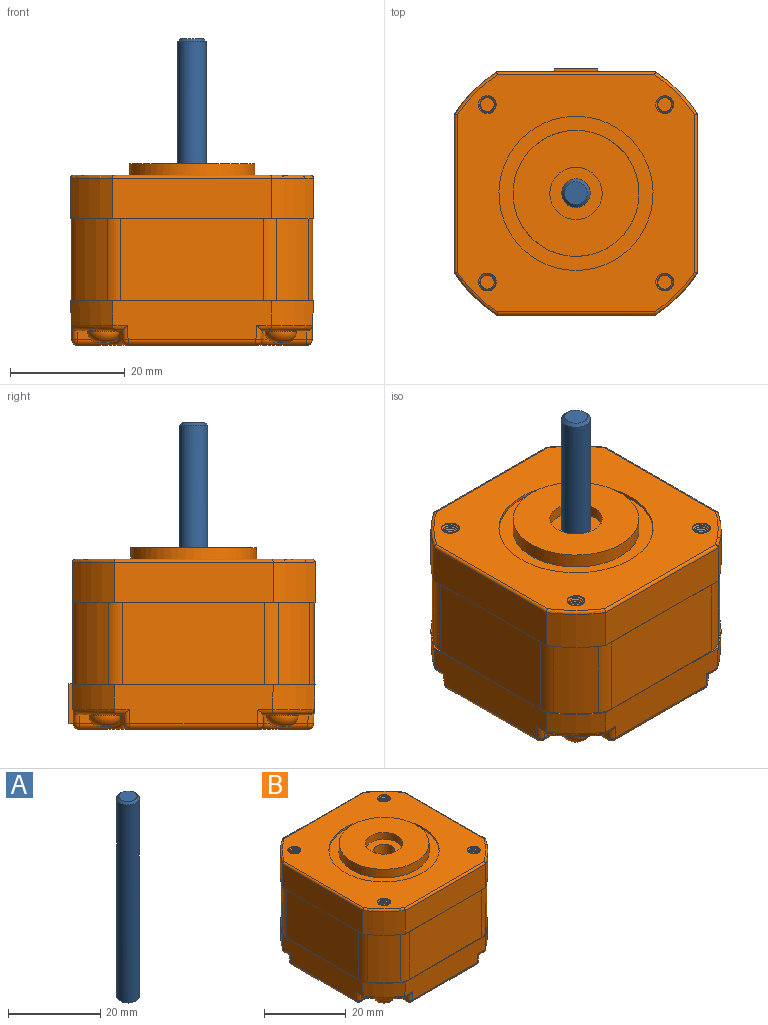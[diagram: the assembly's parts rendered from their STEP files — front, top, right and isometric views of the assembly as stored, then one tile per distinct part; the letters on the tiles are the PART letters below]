
ASSEMBLY  parts=2 mates=1
PART A: 5 faces, bbox 5x5x53.6 mm
  f0: plane 3.98x3.98mm, normal (0,0,1), area 12.4mm2, adj f4
  f1: plane 3.98x3.98mm, normal (0,0,-1), area 12.4mm2, adj f3
  f2: cylinder r=2.5mm len=52.58mm, axis (0,0,1), area 824.4mm2, adj f3,f4
  f3: cone r=2.5mm half-angle=45deg, axis (0,0,1), area 10.1mm2, adj f1,f2
  f4: cone r=1.99mm half-angle=45deg, axis (0,0,-1), area 10.1mm2, adj f0,f2
PART B: 245 faces, bbox 46.1x46.1x31.9 mm
  f0: plane 5.49x4.85mm, normal (0,1,0), area 22.5mm2, adj f228,f229,f230,f231,f232,f233,f237,f239
  f1: plane 27.77x6.84mm, normal (0,1,-0.03), area 121.2mm2, adj f4,f5,f60,f62,f65,f80,f81,f87
  f2: plane 1.69x0.25mm, normal (0,0,-1), area 0.4mm2, adj f6,f46,f222,f226
  f3: plane 1.69x0.25mm, normal (0,0,-1), area 0.4mm2, adj f7,f46,f223,f227
  f4: plane 1.59x0.25mm, normal (0,0,1), area 0.4mm2, adj f1,f6,f222,f226
  f5: plane 1.59x0.25mm, normal (0,0,1), area 0.4mm2, adj f1,f7,f223,f227
  f6: plane 6.61x0.25mm, normal (0,1,0), area 1.7mm2, adj f2,f4,f222,f226
  f7: plane 6.61x0.25mm, normal (0,1,0), area 1.7mm2, adj f3,f5,f223,f227
  f8: plane 0.62x0.62mm, normal (0,0,-1), area 0.3mm2, adj f181,f214,f215
  f9: plane 0.62x0.62mm, normal (0,0,-1), area 0.3mm2, adj f181,f216,f217
  f10: plane 0.62x0.62mm, normal (0,0,-1), area 0.3mm2, adj f181,f218,f219
  f11: plane 0.62x0.62mm, normal (0,0,-1), area 0.3mm2, adj f177,f201,f202
  f12: plane 0.62x0.62mm, normal (0,0,-1), area 0.3mm2, adj f177,f203,f204
  f13: plane 0.62x0.62mm, normal (0,0,-1), area 0.3mm2, adj f177,f205,f206
  f14: plane 0.62x0.62mm, normal (0,0,-1), area 0.3mm2, adj f173,f188,f189
  f15: plane 0.62x0.62mm, normal (0,0,-1), area 0.3mm2, adj f173,f190,f191
  f16: plane 0.62x0.62mm, normal (0,0,-1), area 0.3mm2, adj f173,f192,f193
  f17: plane 7.81x7.81mm, normal (0,0,-1), area 17.4mm2, adj f74,f75,f76,f80,f81,f83,f86,f90
  f18: plane 7.81x7.81mm, normal (0,0,-1), area 17.4mm2, adj f77,f78,f79,f97,f101,f105,f108,f113
  f19: plane 7.81x7.81mm, normal (0,0,-1), area 17.4mm2, adj f68,f69,f70,f87,f91,f94,f98,f102
  f20: plane 41.4x41.4mm, normal (0,0,1), area 1030.3mm2, adj f36,f37,f38,f39,f40,f41,f42,f43
  f21: plane 0.62x0.62mm, normal (0,0,-1), area 0.3mm2, adj f138,f145,f146
  f22: plane 0.62x0.62mm, normal (0,0,-1), area 0.3mm2, adj f138,f147,f148
  f23: plane 0.62x0.62mm, normal (0,0,-1), area 0.3mm2, adj f138,f149,f150
  f24: plane 7.81x7.81mm, normal (0,0,-1), area 17.4mm2, adj f71,f72,f73,f109,f110,f114,f117,f120
  f25: plane 39.91x39.91mm, normal (0,0,-1), area 1280.7mm2, adj f82,f85,f88,f89,f95,f96,f99,f103
  f26: plane 22x22mm, normal (0,0,1), area 314.3mm2, adj f124,f127
  f27: plane 42.42x42.42mm, normal (0,0,-1), area 24.6mm2, adj f28,f29,f30,f31,f32,f33,f34,f35
  f28: cylinder r=25.35mm len=7.33mm, axis (0,0,1), area 73.7mm2, adj f27,f29,f35,f42
  f29: plane 27.77x7.06mm, normal (0,1,0), area 196.1mm2, adj f27,f28,f30,f43
  f30: cylinder r=25.35mm len=7.33mm, axis (0,0,1), area 73.7mm2, adj f27,f29,f31,f41
  f31: plane 27.77x7.06mm, normal (1,0,0), area 196.1mm2, adj f27,f30,f32,f39
  f32: cylinder r=25.35mm len=7.33mm, axis (0,0,1), area 73.7mm2, adj f27,f31,f33,f37
  f33: plane 27.77x7.06mm, normal (0,-1,0), area 196.1mm2, adj f27,f32,f34,f36
  f34: cylinder r=25.35mm len=7.33mm, axis (0,0,1), area 73.7mm2, adj f27,f33,f35,f38
  f35: plane 27.77x7.06mm, normal (-1,0,0), area 196.1mm2, adj f27,f28,f34,f40
  f36: cylinder r=0.51mm len=27.77mm, axis (1,0,0), area 22mm2, adj f20,f33,f37,f38
  f37: torus R=24.84mm, axis (0,0,1), area 8.1mm2, adj f20,f32,f36,f39
  f38: torus R=24.84mm, axis (0,0,1), area 8.1mm2, adj f20,f34,f36,f40
  f39: cylinder r=0.51mm len=27.77mm, axis (0,1,0), area 22mm2, adj f20,f31,f37,f41
  f40: cylinder r=0.51mm len=27.77mm, axis (0,-1,0), area 22mm2, adj f20,f35,f38,f42
  f41: torus R=24.84mm, axis (0,0,1), area 8.1mm2, adj f20,f30,f39,f43
  f42: torus R=24.84mm, axis (0,0,1), area 8.1mm2, adj f20,f28,f40,f43
  f43: cylinder r=0.51mm len=27.77mm, axis (-1,0,0), area 22mm2, adj f20,f29,f41,f42
  f44: cylinder r=25.13mm len=14.33mm, axis (0,0,1), area 112.4mm2, adj f27,f45,f58,f60
  f45: cylinder r=4.01mm len=14.33mm, axis (0,0,1), area 36.2mm2, adj f27,f44,f46,f60
  f46: plane 24.85x14.33mm, normal (0,1,0), area 356mm2, adj f2,f3,f27,f45,f47,f60,f224
  f47: cylinder r=4.01mm len=14.33mm, axis (0,0,1), area 36.2mm2, adj f27,f46,f48,f60
  f48: cylinder r=25.13mm len=14.33mm, axis (0,0,1), area 112.4mm2, adj f27,f47,f49,f60
  f49: cylinder r=4.01mm len=14.33mm, axis (0,0,1), area 36.2mm2, adj f27,f48,f50,f60
  f50: plane 24.85x14.33mm, normal (1,0,0), area 356mm2, adj f27,f49,f51,f60
  f51: cylinder r=4.01mm len=14.33mm, axis (0,0,1), area 36.2mm2, adj f27,f50,f52,f60
  f52: cylinder r=25.13mm len=14.33mm, axis (0,0,1), area 112.4mm2, adj f27,f51,f53,f60
  f53: cylinder r=4.01mm len=14.33mm, axis (0,0,1), area 36.2mm2, adj f27,f52,f54,f60
  f54: plane 24.85x14.33mm, normal (0,-1,0), area 356mm2, adj f27,f53,f55,f60
  f55: cylinder r=4.01mm len=14.33mm, axis (0,0,1), area 36.2mm2, adj f27,f54,f56,f60
  f56: cylinder r=25.13mm len=14.33mm, axis (0,0,1), area 112.4mm2, adj f27,f55,f57,f60
  f57: cylinder r=4.01mm len=14.33mm, axis (0,0,1), area 36.2mm2, adj f27,f56,f59,f60
  f58: cylinder r=4.01mm len=14.33mm, axis (0,0,1), area 36.2mm2, adj f27,f44,f59,f60
  f59: plane 24.85x14.33mm, normal (-1,0,0), area 356mm2, adj f27,f57,f58,f60
  f60: plane 42.42x42.42mm, normal (0,0,1), area 23.6mm2, adj f1,f44,f45,f46,f47,f48,f49,f50
  f61: cone r=25.35mm half-angle=2deg, axis (0,0,1), area 44.6mm2, adj f60,f64,f67,f105
  f62: cone r=25.35mm half-angle=2deg, axis (0,0,1), area 44.6mm2, adj f1,f60,f64,f83
  f63: cone r=25.35mm half-angle=2deg, axis (0,0,1), area 44.6mm2, adj f60,f66,f67,f114
  f64: plane 27.77x6.84mm, normal (-1,0,-0.03), area 176.3mm2, adj f60,f61,f62,f86,f90,f96,f97,f101
  f65: cone r=25.35mm half-angle=2deg, axis (0,0,1), area 44.6mm2, adj f1,f60,f66,f94
  f66: plane 27.77x6.84mm, normal (1,0,-0.03), area 176.3mm2, adj f60,f63,f65,f98,f102,f109,f110,f111
  f67: plane 27.77x6.84mm, normal (0,-1,-0.03), area 176.3mm2, adj f60,f61,f63,f108,f113,f117,f119,f120
  f68: plane 4.47x1.56mm, normal (0,1,-0.03), area 6.9mm2, adj f19,f69,f102,f103
  f69: cone r=3.3mm half-angle=2deg, axis (0,0,-1), area 8.2mm2, adj f19,f68,f70,f99
  f70: plane 4.47x1.56mm, normal (1,0,-0.03), area 6.9mm2, adj f19,f69,f87,f95
  f71: plane 4.47x1.56mm, normal (1,0,-0.03), area 6.9mm2, adj f24,f72,f120,f123
  f72: cone r=3.3mm half-angle=2deg, axis (0,0,-1), area 8.2mm2, adj f24,f71,f73,f121
  f73: plane 4.47x1.56mm, normal (0,-1,-0.03), area 6.9mm2, adj f24,f72,f110,f118
  f74: plane 4.47x1.56mm, normal (-1,0,-0.03), area 6.9mm2, adj f17,f75,f81,f82
  f75: cone r=3.3mm half-angle=2deg, axis (0,0,-1), area 8.2mm2, adj f17,f74,f76,f85
  f76: plane 4.47x1.56mm, normal (0,1,-0.03), area 6.9mm2, adj f17,f75,f89,f90
  f77: cone r=3.3mm half-angle=2deg, axis (0,0,-1), area 8.2mm2, adj f18,f78,f79,f107
  f78: plane 4.47x1.56mm, normal (-1,0,-0.03), area 6.9mm2, adj f18,f77,f112,f113
  f79: plane 4.47x1.56mm, normal (0,-1,-0.03), area 6.9mm2, adj f18,f77,f97,f104
  f80: cylinder r=1.02mm len=2.58mm, axis (-1,0,0), area 3mm2, adj f1,f17,f81,f83
  f81: cylinder r=1.02mm len=2.55mm, axis (-0.03,0.03,1), area 3.1mm2, adj f1,f17,f74,f80,f84
  f82: cylinder r=1.02mm len=4.42mm, axis (0,1,0), area 6.9mm2, adj f25,f74,f84,f85
  f83: torus R=24.18mm, axis (0,0,-1), area 15.3mm2, adj f17,f62,f80,f86,f179
  f84: sphere r=1.02mm, area 1.6mm2, adj f81,f82,f88
  f85: torus R=4.37mm, axis (0,0,1), area 9.2mm2, adj f25,f75,f82,f89
  f86: cylinder r=1.02mm len=2.58mm, axis (0,-1,0), area 3mm2, adj f17,f64,f83,f90
  f87: cylinder r=1.02mm len=2.55mm, axis (-0.03,-0.03,-1), area 3.1mm2, adj f1,f19,f70,f91,f92
  f88: cylinder r=1.02mm len=22.33mm, axis (1,0,0), area 34.9mm2, adj f1,f25,f84,f92
  f89: cylinder r=1.02mm len=4.42mm, axis (1,0,0), area 6.9mm2, adj f25,f76,f85,f93
  f90: cylinder r=1.02mm len=2.55mm, axis (0.03,-0.03,-1), area 3.1mm2, adj f17,f64,f76,f86,f93
  f91: cylinder r=1.02mm len=2.58mm, axis (-1,0,0), area 3mm2, adj f1,f19,f87,f94
  f92: sphere r=1.02mm, area 1.6mm2, adj f87,f88,f95
  f93: sphere r=1.02mm, area 1.6mm2, adj f89,f90,f96
  f94: torus R=24.18mm, axis (0,0,1), area 15.3mm2, adj f19,f65,f91,f98,f171
  f95: cylinder r=1.02mm len=4.42mm, axis (0,-1,0), area 6.9mm2, adj f25,f70,f92,f99
  f96: cylinder r=1.02mm len=22.33mm, axis (0,1,0), area 34.9mm2, adj f25,f64,f93,f100
  f97: cylinder r=1.02mm len=2.55mm, axis (-0.03,-0.03,1), area 3.1mm2, adj f18,f64,f79,f100,f101
  f98: cylinder r=1.02mm len=2.58mm, axis (0,1,0), area 3mm2, adj f19,f66,f94,f102
  f99: torus R=4.37mm, axis (0,0,1), area 9.2mm2, adj f25,f69,f95,f103
  f100: sphere r=1.02mm, area 1.6mm2, adj f96,f97,f104
  f101: cylinder r=1.02mm len=2.58mm, axis (0,-1,0), area 3mm2, adj f18,f64,f97,f105
  f102: cylinder r=1.02mm len=2.55mm, axis (0.03,0.03,1), area 3.1mm2, adj f19,f66,f68,f98,f106
  f103: cylinder r=1.02mm len=4.42mm, axis (1,0,0), area 6.9mm2, adj f25,f68,f99,f106
  f104: cylinder r=1.02mm len=4.42mm, axis (-1,0,0), area 6.9mm2, adj f25,f79,f100,f107
  f105: torus R=24.18mm, axis (0,0,-1), area 15.3mm2, adj f18,f61,f101,f108,f175
  f106: sphere r=1.02mm, area 1.6mm2, adj f102,f103,f111
  f107: torus R=4.37mm, axis (0,0,1), area 9.2mm2, adj f25,f77,f104,f112
  f108: cylinder r=1.02mm len=2.58mm, axis (1,0,0), area 3mm2, adj f18,f67,f105,f113
  f109: cylinder r=1.02mm len=2.58mm, axis (0,1,0), area 3mm2, adj f24,f66,f110,f114
  f110: cylinder r=1.02mm len=2.55mm, axis (-0.03,0.03,-1), area 3.1mm2, adj f24,f66,f73,f109,f115
  f111: cylinder r=1.02mm len=22.33mm, axis (0,-1,0), area 34.9mm2, adj f25,f66,f106,f115
  f112: cylinder r=1.02mm len=4.42mm, axis (0,1,0), area 6.9mm2, adj f25,f78,f107,f116
  f113: cylinder r=1.02mm len=2.55mm, axis (0.03,0.03,-1), area 3.1mm2, adj f18,f67,f78,f108,f116
  f114: torus R=24.18mm, axis (0,0,-1), area 15.3mm2, adj f24,f63,f109,f117,f136
  f115: sphere r=1.02mm, area 1.6mm2, adj f110,f111,f118
  f116: sphere r=1.02mm, area 1.6mm2, adj f112,f113,f119
  f117: cylinder r=1.02mm len=2.58mm, axis (1,0,0), area 3mm2, adj f24,f67,f114,f120
  f118: cylinder r=1.02mm len=4.42mm, axis (-1,0,0), area 6.9mm2, adj f25,f73,f115,f121
  f119: cylinder r=1.02mm len=22.33mm, axis (-1,0,0), area 34.9mm2, adj f25,f67,f116,f122
  f120: cylinder r=1.02mm len=2.55mm, axis (0.03,-0.03,1), area 3.1mm2, adj f24,f67,f71,f117,f122
  f121: torus R=4.37mm, axis (0,0,1), area 9.2mm2, adj f25,f72,f118,f123
  f122: sphere r=1.02mm, area 1.6mm2, adj f119,f120,f123
  f123: cylinder r=1.02mm len=4.42mm, axis (0,-1,0), area 6.9mm2, adj f25,f71,f121,f122
  f124: cylinder r=11mm len=22mm, axis (0,0,-1), area 175.5mm2, adj f26,f128
  f125: cylinder r=2.5mm len=29.72mm, axis (0,0,1), area 466mm2, adj f25,f126
  f126: plane 9.14x9.14mm, normal (0,0,1), area 46.1mm2, adj f125,f127
  f127: cylinder r=4.57mm len=9.14mm, axis (0,0,1), area 58.4mm2, adj f26,f126
  f128: plane 26.92x26.92mm, normal (0,0,1), area 189.3mm2, adj f124,f129
  f129: cylinder r=13.46mm len=26.92mm, axis (0,0,1), area 43mm2, adj f20,f128
  f130: cone r=1.55mm half-angle=45deg, axis (0,0,1), area 2.6mm2, adj f20,f132,f133,f134,f135
  f131: plane 2.87x2.83mm, normal (0,0,1), area 5.7mm2, adj f132,f133,f134,f135
  f132: bspline ~4.01x3.53mm, area 19.4mm2, adj f130,f131,f133,f135
  f133: bspline ~3.88x2.84mm, area 6.7mm2, adj f130,f131,f132,f134
  f134: bspline ~4.17x3.53mm, area 19.4mm2, adj f130,f131,f133,f135
  f135: cylinder r=1.5mm len=3.76mm, axis (0,0,1), area 7.3mm2, adj f130,f131,f132,f134
  f136: plane 2.3x2.3mm, normal (0,0,1), area 1.1mm2, adj f114,f137
  f137: cylinder r=2.75mm len=5.5mm, axis (0,0,1), area 2.2mm2, adj f24,f136,f138
  f138: torus R=0.84mm, axis (0,0,1), area 37.5mm2, adj f21,f22,f23,f137,f139,f140,f141,f142
  f139: plane 0.62x0.62mm, normal (0,0,-1), area 0.3mm2, adj f138,f144,f151
  f140: plane 1.41x0.41mm, normal (0,-1,0), area 0.6mm2, adj f138,f144,f145,f152
  f141: plane 1.41x0.41mm, normal (1,0,0), area 0.6mm2, adj f138,f146,f147,f152
  f142: plane 1.41x0.41mm, normal (0,1,0), area 0.6mm2, adj f138,f148,f149,f152
  f143: plane 1.42x0.41mm, normal (-1,0,0), area 0.6mm2, adj f138,f150,f151,f152
  f144: plane 1.56x1.34mm, normal (-1,0,0), area 1.9mm2, adj f138,f139,f140,f151,f152
  f145: plane 1.56x1.33mm, normal (1,0,0), area 1.9mm2, adj f21,f138,f140,f146,f152
  f146: plane 1.56x1.34mm, normal (0,-1,0), area 1.9mm2, adj f21,f138,f141,f145,f152
  f147: plane 1.56x1.33mm, normal (0,1,0), area 1.9mm2, adj f22,f138,f141,f148,f152
  f148: plane 1.56x1.34mm, normal (1,0,0), area 1.9mm2, adj f22,f138,f142,f147,f152
  f149: plane 1.56x1.33mm, normal (-1,0,0), area 1.9mm2, adj f23,f138,f142,f150,f152
  f150: plane 1.56x1.34mm, normal (0,1,0), area 1.9mm2, adj f23,f138,f143,f149,f152
  f151: plane 1.56x1.33mm, normal (0,-1,0), area 1.9mm2, adj f138,f139,f143,f144,f152
  f152: plane 3x3mm, normal (0,0,-1), area 2.3mm2, adj f140,f141,f142,f143,f144,f145,f146,f147
  f153: cone r=1.55mm half-angle=45deg, axis (0,0,1), area 2.6mm2, adj f20,f155,f156,f157,f158
  f154: plane 2.87x2.83mm, normal (0,0,1), area 5.7mm2, adj f155,f156,f157,f158
  f155: bspline ~4.01x3.53mm, area 19.4mm2, adj f153,f154,f156,f158
  f156: bspline ~3.88x2.84mm, area 6.7mm2, adj f153,f154,f155,f157
  f157: bspline ~4.17x3.53mm, area 19.4mm2, adj f153,f154,f156,f158
  f158: cylinder r=1.5mm len=3.76mm, axis (0,0,1), area 7.3mm2, adj f153,f154,f155,f157
  f159: cone r=1.55mm half-angle=45deg, axis (0,0,1), area 2.6mm2, adj f20,f161,f162,f163,f164
  f160: plane 2.87x2.83mm, normal (0,0,1), area 5.7mm2, adj f161,f162,f163,f164
  f161: bspline ~4.01x3.53mm, area 19.4mm2, adj f159,f160,f162,f164
  f162: bspline ~3.88x2.84mm, area 6.7mm2, adj f159,f160,f161,f163
  f163: bspline ~4.17x3.53mm, area 19.4mm2, adj f159,f160,f162,f164
  f164: cylinder r=1.5mm len=3.76mm, axis (0,0,1), area 7.3mm2, adj f159,f160,f161,f163
  f165: cone r=1.55mm half-angle=45deg, axis (0,0,1), area 2.6mm2, adj f20,f167,f168,f169,f170
  f166: plane 2.87x2.83mm, normal (0,0,1), area 5.7mm2, adj f167,f168,f169,f170
  f167: bspline ~4.01x3.53mm, area 19.4mm2, adj f165,f166,f168,f170
  f168: bspline ~3.88x2.84mm, area 6.7mm2, adj f165,f166,f167,f169
  f169: bspline ~4.17x3.53mm, area 19.4mm2, adj f165,f166,f168,f170
  f170: cylinder r=1.5mm len=3.76mm, axis (0,0,1), area 7.3mm2, adj f165,f166,f167,f169
  f171: plane 2.3x2.3mm, normal (0,0,1), area 1.1mm2, adj f94,f172
  f172: cylinder r=2.75mm len=5.5mm, axis (0,0,1), area 2.2mm2, adj f19,f171,f173
  f173: torus R=0.84mm, axis (0,0,1), area 37.5mm2, adj f14,f15,f16,f172,f174,f183,f184,f185
  f174: plane 0.62x0.62mm, normal (0,0,-1), area 0.3mm2, adj f173,f187,f194
  f175: plane 2.3x2.3mm, normal (0,0,1), area 1.1mm2, adj f105,f176
  f176: cylinder r=2.75mm len=5.5mm, axis (0,0,1), area 2.2mm2, adj f18,f175,f177
  f177: torus R=0.84mm, axis (0,0,1), area 37.5mm2, adj f11,f12,f13,f176,f178,f196,f197,f198
  f178: plane 0.62x0.62mm, normal (0,0,-1), area 0.3mm2, adj f177,f200,f207
  f179: plane 2.3x2.3mm, normal (0,0,1), area 1.1mm2, adj f83,f180
  f180: cylinder r=2.75mm len=5.5mm, axis (0,0,1), area 2.2mm2, adj f17,f179,f181
  f181: torus R=0.84mm, axis (0,0,1), area 37.5mm2, adj f8,f9,f10,f180,f182,f209,f210,f211
  f182: plane 0.62x0.62mm, normal (0,0,-1), area 0.3mm2, adj f181,f213,f220
  f183: plane 1.41x0.41mm, normal (0,-1,0), area 0.6mm2, adj f173,f187,f188,f195
  f184: plane 1.41x0.41mm, normal (1,0,0), area 0.6mm2, adj f173,f189,f190,f195
  f185: plane 1.41x0.41mm, normal (0,1,0), area 0.6mm2, adj f173,f191,f192,f195
  f186: plane 1.42x0.41mm, normal (-1,0,0), area 0.6mm2, adj f173,f193,f194,f195
  f187: plane 1.56x1.34mm, normal (-1,0,0), area 1.9mm2, adj f173,f174,f183,f194,f195
  f188: plane 1.56x1.33mm, normal (1,0,0), area 1.9mm2, adj f14,f173,f183,f189,f195
  f189: plane 1.56x1.34mm, normal (0,-1,0), area 1.9mm2, adj f14,f173,f184,f188,f195
  f190: plane 1.56x1.33mm, normal (0,1,0), area 1.9mm2, adj f15,f173,f184,f191,f195
  f191: plane 1.56x1.34mm, normal (1,0,0), area 1.9mm2, adj f15,f173,f185,f190,f195
  f192: plane 1.56x1.33mm, normal (-1,0,0), area 1.9mm2, adj f16,f173,f185,f193,f195
  f193: plane 1.56x1.34mm, normal (0,1,0), area 1.9mm2, adj f16,f173,f186,f192,f195
  f194: plane 1.56x1.33mm, normal (0,-1,0), area 1.9mm2, adj f173,f174,f186,f187,f195
  f195: plane 3x3mm, normal (0,0,-1), area 2.3mm2, adj f183,f184,f185,f186,f187,f188,f189,f190
  f196: plane 1.41x0.41mm, normal (0,-1,0), area 0.6mm2, adj f177,f200,f201,f208
  f197: plane 1.41x0.41mm, normal (1,0,0), area 0.6mm2, adj f177,f202,f203,f208
  f198: plane 1.41x0.41mm, normal (0,1,0), area 0.6mm2, adj f177,f204,f205,f208
  f199: plane 1.42x0.41mm, normal (-1,0,0), area 0.6mm2, adj f177,f206,f207,f208
  f200: plane 1.56x1.34mm, normal (-1,0,0), area 1.9mm2, adj f177,f178,f196,f207,f208
  f201: plane 1.56x1.33mm, normal (1,0,0), area 1.9mm2, adj f11,f177,f196,f202,f208
  f202: plane 1.56x1.34mm, normal (0,-1,0), area 1.9mm2, adj f11,f177,f197,f201,f208
  f203: plane 1.56x1.33mm, normal (0,1,0), area 1.9mm2, adj f12,f177,f197,f204,f208
  f204: plane 1.56x1.34mm, normal (1,0,0), area 1.9mm2, adj f12,f177,f198,f203,f208
  f205: plane 1.56x1.33mm, normal (-1,0,0), area 1.9mm2, adj f13,f177,f198,f206,f208
  f206: plane 1.56x1.34mm, normal (0,1,0), area 1.9mm2, adj f13,f177,f199,f205,f208
  f207: plane 1.56x1.33mm, normal (0,-1,0), area 1.9mm2, adj f177,f178,f199,f200,f208
  f208: plane 3x3mm, normal (0,0,-1), area 2.3mm2, adj f196,f197,f198,f199,f200,f201,f202,f203
  f209: plane 1.41x0.41mm, normal (0,-1,0), area 0.6mm2, adj f181,f213,f214,f221
  f210: plane 1.41x0.41mm, normal (1,0,0), area 0.6mm2, adj f181,f215,f216,f221
  f211: plane 1.41x0.41mm, normal (0,1,0), area 0.6mm2, adj f181,f217,f218,f221
  f212: plane 1.42x0.41mm, normal (-1,0,0), area 0.6mm2, adj f181,f219,f220,f221
  f213: plane 1.56x1.34mm, normal (-1,0,0), area 1.9mm2, adj f181,f182,f209,f220,f221
  f214: plane 1.56x1.33mm, normal (1,0,0), area 1.9mm2, adj f8,f181,f209,f215,f221
  f215: plane 1.56x1.34mm, normal (0,-1,0), area 1.9mm2, adj f8,f181,f210,f214,f221
  f216: plane 1.56x1.33mm, normal (0,1,0), area 1.9mm2, adj f9,f181,f210,f217,f221
  f217: plane 1.56x1.34mm, normal (1,0,0), area 1.9mm2, adj f9,f181,f211,f216,f221
  f218: plane 1.56x1.33mm, normal (-1,0,0), area 1.9mm2, adj f10,f181,f211,f219,f221
  f219: plane 1.56x1.34mm, normal (0,1,0), area 1.9mm2, adj f10,f181,f212,f218,f221
  f220: plane 1.56x1.33mm, normal (0,-1,0), area 1.9mm2, adj f181,f182,f212,f213,f221
  f221: plane 3x3mm, normal (0,0,-1), area 2.3mm2, adj f209,f210,f211,f212,f213,f214,f215,f216
  f222: plane 6.61x1.82mm, normal (1,0,0), area 11.2mm2, adj f1,f2,f4,f6,f60
  f223: plane 6.61x1.82mm, normal (-1,0,0), area 11.2mm2, adj f1,f3,f5,f7,f60
  f224: plane 7.62x0.13mm, normal (0,0,1), area 1mm2, adj f46,f226,f227,f234
  f225: plane 7.62x6.99mm, normal (0,1,0), area 27.8mm2, adj f226,f227,f228,f229,f230,f231,f232,f233
  f226: plane 6.99x2.36mm, normal (-1,0,0), area 15.9mm2, adj f1,f2,f4,f6,f224,f225,f234,f235
  f227: plane 6.99x2.36mm, normal (1,0,0), area 15.9mm2, adj f1,f3,f5,f7,f224,f225,f234,f235
  f228: plane 4.41x2.36mm, normal (0,0,-1), area 10.4mm2, adj f0,f225,f229,f233
  f229: plane 2.36x1.08mm, normal (-0.71,0,-0.71), area 3.6mm2, adj f0,f225,f228,f230
  f230: plane 3.77x2.36mm, normal (-1,0,0), area 8.9mm2, adj f0,f225,f229,f231
  f231: plane 4.41x2.36mm, normal (0,0,1), area 10.4mm2, adj f0,f225,f230,f232
  f232: plane 2.36x1.08mm, normal (0.71,0,0.71), area 3.6mm2, adj f0,f225,f231,f233
  f233: plane 3.77x2.36mm, normal (1,0,0), area 8.9mm2, adj f0,f225,f228,f232
  f234: plane 7.62x0.19mm, normal (0,-1,0.03), area 1.4mm2, adj f224,f226,f227,f235
  f235: plane 7.62x0.54mm, normal (0,0,1), area 4.1mm2, adj f225,f226,f227,f234
  f236: plane 7.62x0.79mm, normal (0,0,-1), area 6mm2, adj f1,f225,f226,f227
  f237: cylinder r=0.48mm len=1.93mm, axis (0,-1,0), area 5.9mm2, adj f0,f238
  f238: plane 0.97x0.97mm, normal (0,1,0), area 0.7mm2, adj f237
  f239: cylinder r=0.48mm len=1.93mm, axis (0,-1,0), area 5.9mm2, adj f0,f240
  f240: plane 0.97x0.97mm, normal (0,1,0), area 0.7mm2, adj f239
  f241: cylinder r=0.48mm len=1.93mm, axis (0,-1,0), area 5.9mm2, adj f0,f242
  f242: plane 0.97x0.97mm, normal (0,1,0), area 0.7mm2, adj f241
  f243: cylinder r=0.48mm len=1.93mm, axis (0,-1,0), area 5.9mm2, adj f0,f244
  f244: plane 0.97x0.97mm, normal (0,1,0), area 0.7mm2, adj f243
PLACE A at identity
PLACE B at identity fixed
MATE revolute A.f2 <-> B.f124  axis (0,0,1) through (0,0,23.88)mm
